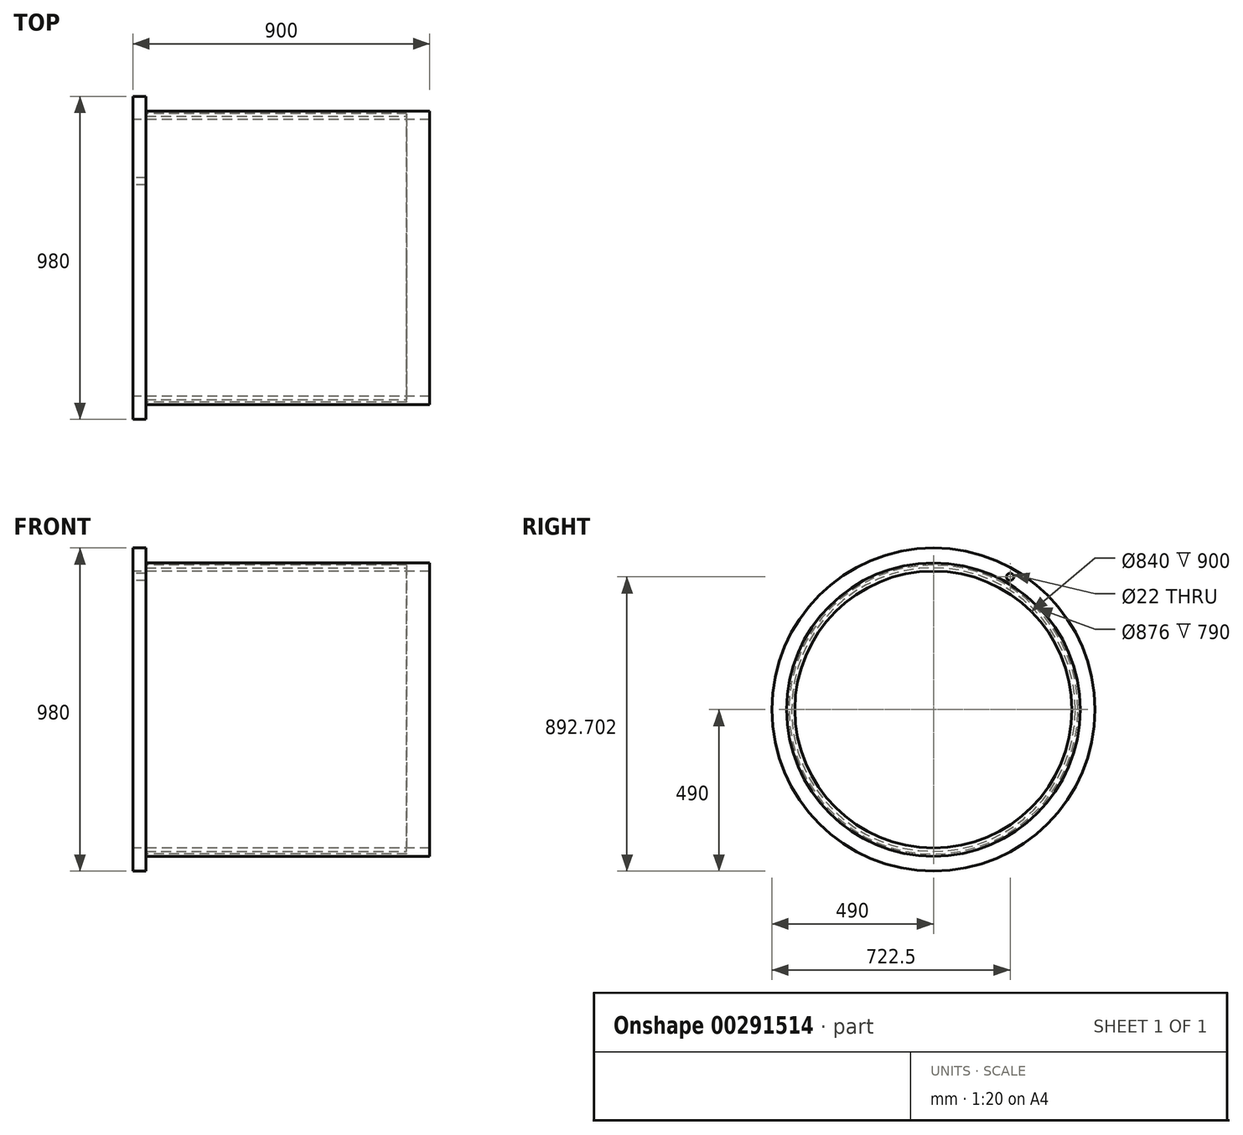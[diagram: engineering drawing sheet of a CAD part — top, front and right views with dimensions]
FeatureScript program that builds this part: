
annotation { "Feature Type Name" : "Feature", "Feature Type Description" : "" }
export const myFeature = defineFeature(function(context is Context, id is Id, definition is map)
    precondition{}
    {
        {
            var Q0;
            Q0=qCreatedBy(makeId("Front.planeOp"),FACE);
            var sketch = newSketch(context, id + "F0", { "sketchPlane" : qUnion([Q0])});
            skLineSegment(sketch, "E0", {"start": v(-450, 420) * mm, "end": v(450, 420) * mm});
            skLineSegment(sketch, "E1", {"start": v(450, 420) * mm, "end": v(450, 445) * mm});
            skLineSegment(sketch, "E2", {"start": v(450, 445) * mm, "end": v(-410, 445) * mm});
            skLineSegment(sketch, "E3", {"start": v(-410, 445) * mm, "end": v(-410, 490) * mm});
            skLineSegment(sketch, "E4", {"start": v(-410, 490) * mm, "end": v(-450, 490) * mm});
            skLineSegment(sketch, "E5", {"start": v(-450, 490) * mm, "end": v(-450, 420) * mm});
            skLineSegment(sketch, "E6", {"start": v(-377, 0) * mm, "end": v(233.81, 0) * mm});
            skLineSegment(sketch, "E7.bottom", {"start": v(-410, 438) * mm, "end": v(380, 438) * mm});
            skLineSegment(sketch, "E7.top", {"start": v(-410, 432) * mm, "end": v(380, 432) * mm});
            skLineSegment(sketch, "E7.left", {"start": v(-410, 438) * mm, "end": v(-410, 432) * mm});
            skLineSegment(sketch, "E7.right", {"start": v(380, 438) * mm, "end": v(380, 432) * mm});
            skSolve(sketch);
        }
        {
            var Q0;
            Q0=makeQuery(id+"F0.imprint","IMPRINT",FACE,{"disambiguationData":[TD([[makeQuery(id+"F0.imprint","IMPRINT",EDGE,{"derivedFrom":sQuery(id+"F0.wireOp",EDGE,"E0")}),1.0]])]});
            var Q1;
            Q1=sQuery(id+"F0.wireOp",EDGE,"E6");
            revolve(context, id + "F1", {"entities" : qUnion([Q0]), "axis" : qUnion([Q1]), "revolveType" : RevolveType.FULL});
        }
        {
            var Q0;
            Q0=qCreatedBy(makeId("Front.planeOp"),FACE);
            var sketch = newSketch(context, id + "F2", { "sketchPlane" : qUnion([Q0])});
            skLineSegment(sketch, "E8.bottom", {"start": v(-410, 438) * mm, "end": v(380, 438) * mm});
            skLineSegment(sketch, "E8.top", {"start": v(-410, 430) * mm, "end": v(380, 430) * mm});
            skLineSegment(sketch, "E8.left", {"start": v(-410, 438) * mm, "end": v(-410, 430) * mm});
            skLineSegment(sketch, "E8.right", {"start": v(380, 438) * mm, "end": v(380, 430) * mm});
            skLineSegment(sketch, "E9", {"start": v(-725.47, 0) * mm, "end": v(403.89, 0) * mm});
            skSolve(sketch);
        }
        {
            var Q0;
            Q0 = qSketchRegion(id + "F2", true);
            var Q1;
            Q1=sQuery(id+"F2.wireOp",EDGE,"E9");
            revolve(context, id + "F3", {"operationType" : NewBodyOperationType.REMOVE, "entities" : qUnion([Q0]), "axis" : qUnion([Q1]), "revolveType" : RevolveType.FULL, "oppositeDirection" : true});
        }
        {
            var Q0;
            Q0=makeQuery(id+"F1.opRevolve","SWEPT_FACE",FACE,{"disambiguationData":[OSD([sQuery(id+"F0.wireOp",EDGE,"E5")])]});
            var sketch = newSketch(context, id + "F4", { "sketchPlane" : qUnion([Q0])});
            skPoint(sketch, "E10", {"position": v(-232.5, 402.7) * mm});
            skLineSegment(sketch, "E11", {"start": v(-232.5, 402.7) * mm, "end": v(0, 0) * mm});
            skCircle(sketch, "E12", {"center": v(0, 0) * mm, "radius": 465 * mm});
            skLineSegment(sketch, "E13", {"start": v(0, 0) * mm, "end": v(0, 465) * mm});
            skSolve(sketch);
        }
        {
            var Q0;
            Q0=sQuery(id+"F4.wireOp",VERTEX,"E10");
            var Q1;
            Q1=makeQuery(id+"F1.opRevolve","SWEPT_BODY",BODY,{"disambiguationData":[OSD([sQuery(id+"F0.wireOp",EDGE,"E0"),sQuery(id+"F0.wireOp",EDGE,"E1"),sQuery(id+"F0.wireOp",EDGE,"E2"),sQuery(id+"F0.wireOp",EDGE,"E3"),sQuery(id+"F0.wireOp",EDGE,"E4"),sQuery(id+"F0.wireOp",EDGE,"E5"),sQuery(id+"F0.wireOp",EDGE,"E7.bottom"),sQuery(id+"F0.wireOp",EDGE,"E7.top"),sQuery(id+"F0.wireOp",EDGE,"E7.left"),sQuery(id+"F0.wireOp",EDGE,"E7.right")])]});
            hole(context, id + "F5", {"style" : HoleStyle.SIMPLE, "endStyle" : HoleEndStyle.THROUGH, "standardTappedOrClearance" : lookupTablePath({ "standard" : "ISO", "fit" : "Normal", "size" : "M20", "type" : "Clearance" }), "standardBlindInLast" : lookupTablePath({ "fit" : "Standard", "standard" : "ISO", "size" : "M20", "type" : "Clearance" }), "holeDiameter" : 22 * mm, "tappedDepth" : 12 * mm, "tapClearance" : 3, "locations" : qUnion([Q0]), "scope" : qUnion([Q1])});
        }
    });
